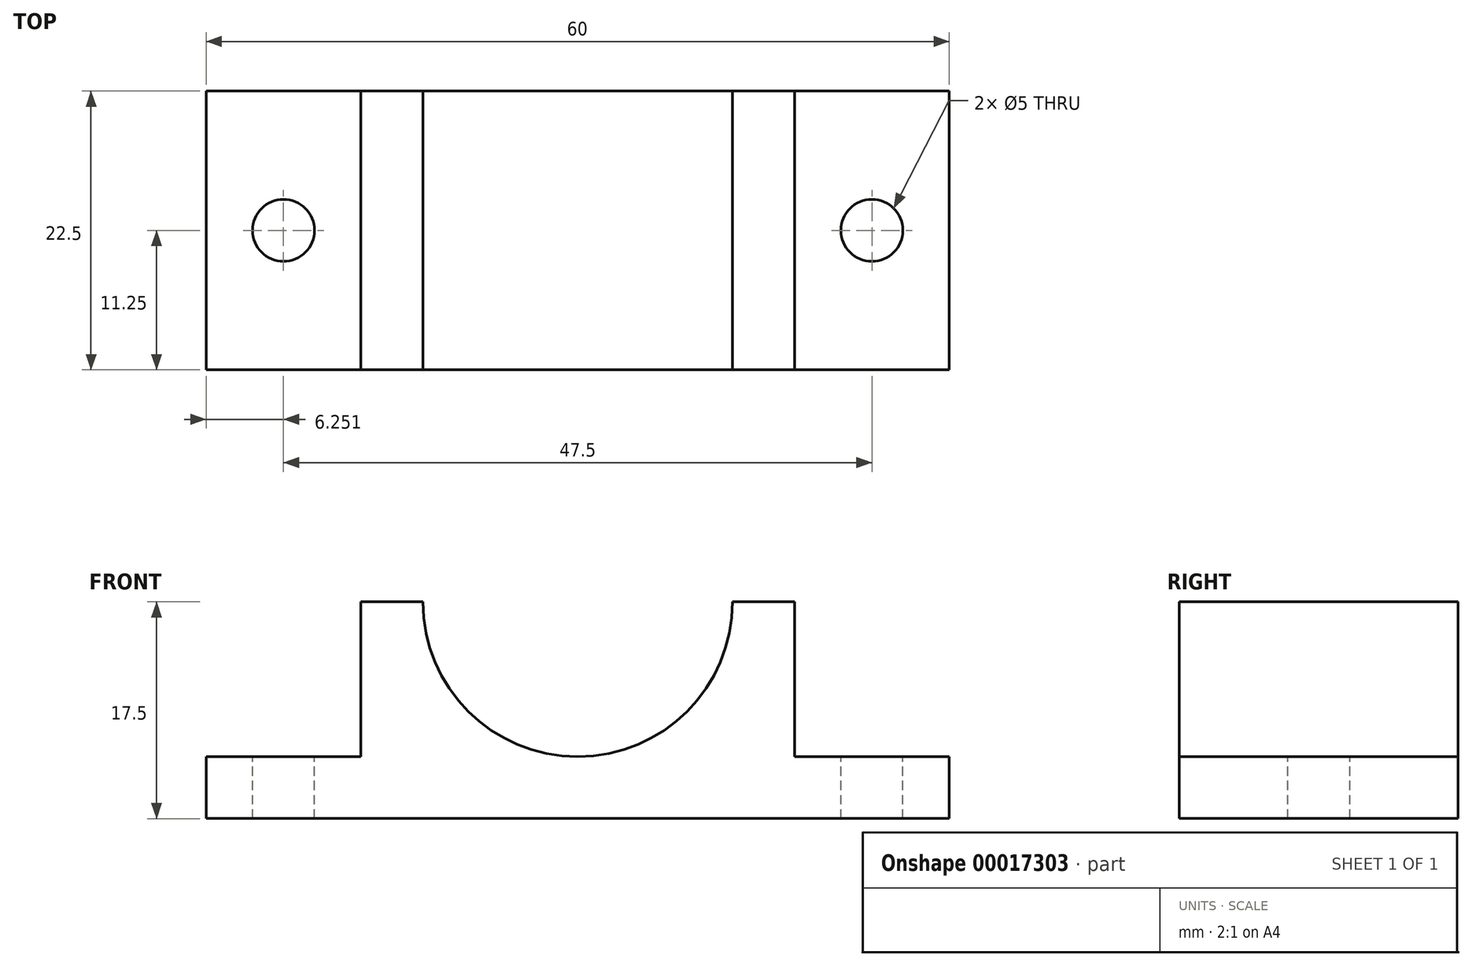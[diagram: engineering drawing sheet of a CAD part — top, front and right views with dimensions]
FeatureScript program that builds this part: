
annotation { "Feature Type Name" : "Feature", "Feature Type Description" : "" }
export const myFeature = defineFeature(function(context is Context, id is Id, definition is map)
    precondition{}
    {
        {
            var Q0;
            Q0=qCreatedBy(makeId("Front.planeOp"),FACE);
            var sketch = newSketch(context, id + "F0", { "sketchPlane" : qUnion([Q0])});
            skLineSegment(sketch, "E0", {"start": v(-34.47, -4.27) * mm, "end": v(25.53, -4.27) * mm});
            skLineSegment(sketch, "E1", {"start": v(25.53, -4.27) * mm, "end": v(25.53, 0.73) * mm});
            skLineSegment(sketch, "E2", {"start": v(25.53, 0.73) * mm, "end": v(13.03, 0.73) * mm});
            skLineSegment(sketch, "E3", {"start": v(13.03, 0.73) * mm, "end": v(13.03, 13.23) * mm});
            skLineSegment(sketch, "E4", {"start": v(-34.47, -4.27) * mm, "end": v(-34.47, 0.73) * mm});
            skLineSegment(sketch, "E5", {"start": v(-34.47, 0.73) * mm, "end": v(-21.97, 0.73) * mm});
            skLineSegment(sketch, "E6", {"start": v(-21.97, 0.73) * mm, "end": v(-21.97, 13.23) * mm});
            skArc(sketch, "E7", {"start": v(-16.97, 13.23) * mm, "mid": v(-4.47, 0.73) * mm, "end": v(8.03, 13.23) * mm});
            skLineSegment(sketch, "E8", {"start": v(-21.97, 13.23) * mm, "end": v(-16.97, 13.23) * mm});
            skLineSegment(sketch, "E9", {"start": v(8.03, 13.23) * mm, "end": v(13.03, 13.23) * mm});
            skSolve(sketch);
        }
        {
            var Q0;
            Q0=makeQuery(id+"F0.imprint","IMPRINT",FACE,{"disambiguationData":[TD([[makeQuery(id+"F0.imprint","IMPRINT",EDGE,{"derivedFrom":sQuery(id+"F0.wireOp",EDGE,"E0")}),1.0]])]});
            extrude(context, id + "F1", {"entities" : qUnion([Q0]), "depth" : 22.5 * mm});
        }
        {
            var Q0;
            Q0=makeQuery(id+"F1.opExtrude","SWEPT_FACE",FACE,{"disambiguationData":[OSD([sQuery(id+"F0.wireOp",EDGE,"E2")])]});
            var sketch = newSketch(context, id + "F2", { "sketchPlane" : qUnion([Q0])});
            skLineSegment(sketch, "E10", {"start": v(25.53, -22.5) * mm, "end": v(25.53, 0) * mm});
            skLineSegment(sketch, "E11", {"start": v(13.03, -22.5) * mm, "end": v(25.53, -22.5) * mm});
            skCircle(sketch, "E12", {"center": v(19.28, -11.25) * mm, "radius": 2.5 * mm});
            skSolve(sketch);
        }
        {
            var Q0;
            Q0=makeQuery(id+"F2.imprint","IMPRINT",FACE,{"disambiguationData":[TD([[makeQuery(id+"F2.imprint","IMPRINT",EDGE,{"derivedFrom":sQuery(id+"F2.wireOp",EDGE,"E12")}),1.0]])]});
            extrude(context, id + "F3", {"entities" : qUnion([Q0]), "operationType" : NewBodyOperationType.REMOVE, "oppositeDirection" : true, "depth" : 25 * mm});
        }
        {
            var Q0;
            Q0=makeQuery(id+"F1.opExtrude","SWEPT_FACE",FACE,{"disambiguationData":[OSD([sQuery(id+"F0.wireOp",EDGE,"E5")])]});
            var sketch = newSketch(context, id + "F4", { "sketchPlane" : qUnion([Q0])});
            skLineSegment(sketch, "E13", {"start": v(-21.97, -22.5) * mm, "end": v(-21.97, 0) * mm});
            skLineSegment(sketch, "E14", {"start": v(-34.47, -22.5) * mm, "end": v(-21.97, -22.5) * mm});
            skCircle(sketch, "E15", {"center": v(-28.22, -11.25) * mm, "radius": 2.5 * mm});
            skSolve(sketch);
        }
        {
            var Q0;
            Q0=makeQuery(id+"F4.imprint","IMPRINT",FACE,{"disambiguationData":[TD([[makeQuery(id+"F4.imprint","IMPRINT",EDGE,{"derivedFrom":sQuery(id+"F4.wireOp",EDGE,"E15")}),1.0]])]});
            extrude(context, id + "F5", {"entities" : qUnion([Q0]), "operationType" : NewBodyOperationType.REMOVE, "oppositeDirection" : true, "depth" : 25 * mm});
        }
    });
